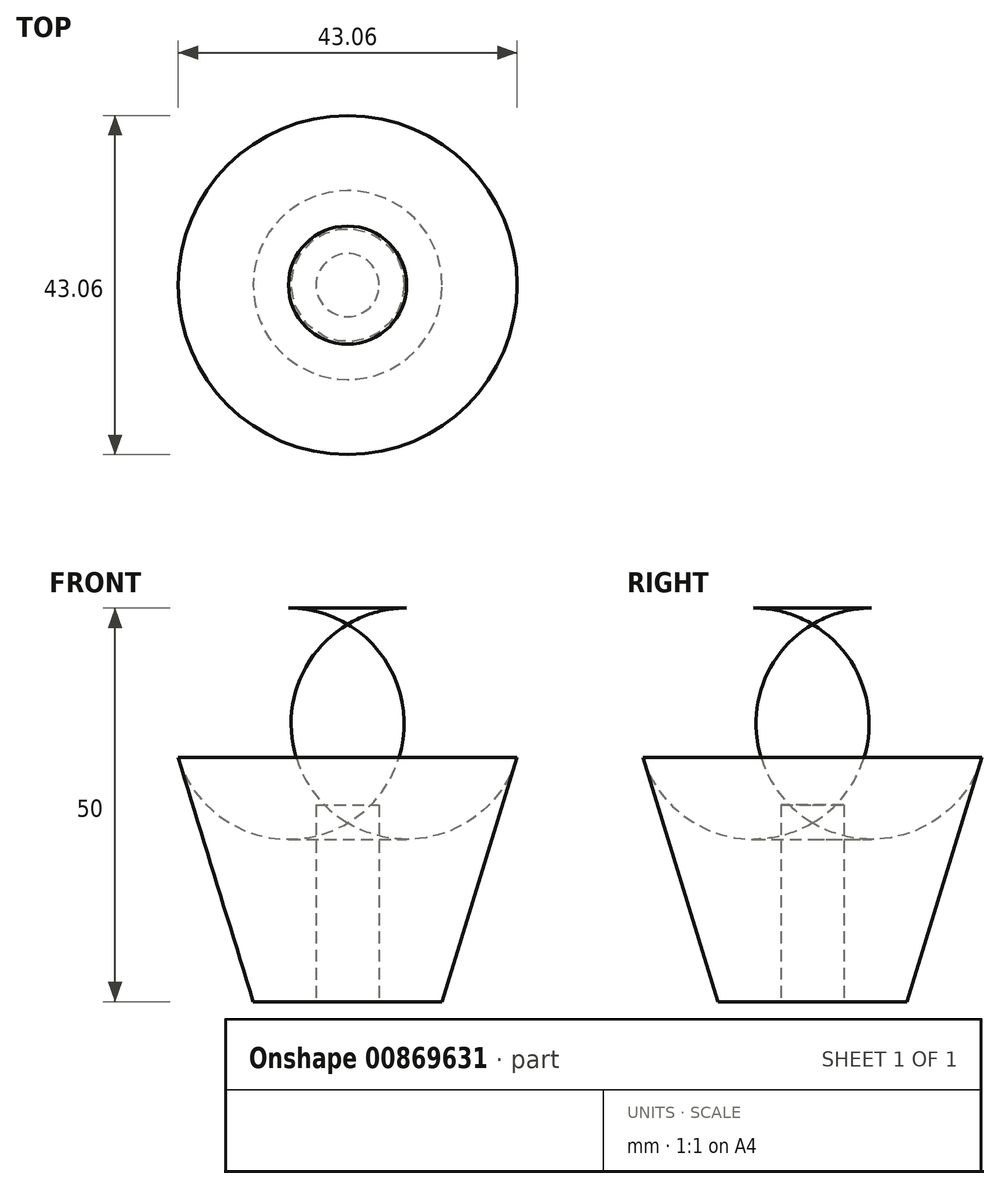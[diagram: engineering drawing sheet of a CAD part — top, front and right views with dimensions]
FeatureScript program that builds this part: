
annotation { "Feature Type Name" : "Feature", "Feature Type Description" : "" }
export const myFeature = defineFeature(function(context is Context, id is Id, definition is map)
    precondition{}
    {
        {
            var Q0;
            Q0=qCreatedBy(makeId("Front.planeOp"),FACE);
            var sketch = newSketch(context, id + "F0", { "sketchPlane" : qUnion([Q0])});
            skLineSegment(sketch, "E0", {"start": v(0, 0) * mm, "end": v(0, 50) * mm});
            skLineSegment(sketch, "E1", {"start": v(0, 50) * mm, "end": v(7.5, 50) * mm});
            skLineSegment(sketch, "E2", {"start": v(0, 0) * mm, "end": v(4, 0) * mm});
            skLineSegment(sketch, "E3", {"start": v(4, 0) * mm, "end": v(4, 25) * mm});
            skPoint(sketch, "E3.endSnap0", {"position": v(0, 25) * mm});
            skLineSegment(sketch, "E4", {"start": v(4, 25) * mm, "end": v(0, 25) * mm});
            skLineSegment(sketch, "E5", {"start": v(4, 0) * mm, "end": v(12, 0) * mm});
            skLineSegment(sketch, "E6", {"start": v(0, 25) * mm, "end": v(0, 31) * mm});
            skArc(sketch, "E7", {"start": v(21.53, 31) * mm, "mid": v(19.31, 44.04) * mm, "end": v(7.5, 50) * mm});
            skLineSegment(sketch, "E8", {"start": v(12, 0) * mm, "end": v(21.53, 31) * mm});
            skLineSegment(sketch, "E9", {"start": v(0, 31) * mm, "end": v(21.53, 31) * mm});
            skPoint(sketch, "E10.endSnap0", {"position": v(8, 0) * mm});
            skSolve(sketch);
        }
        {
            var Q0;
            {var subQ2=sQuery(id+"F0.wireOp",EDGE,"E1");Q0=makeQuery(id+"F0.imprint","IMPRINT",FACE,{"disambiguationData":[TD([[makeQuery(id+"F0.imprint","IMPRINT",EDGE,{"derivedFrom":subQ2}),-1.0]])]});}
            var Q1;
            Q1=makeQuery(id+"F0.imprint","IMPRINT",FACE,{"disambiguationData":[TD([[makeQuery(id+"F0.imprint","IMPRINT",EDGE,{"derivedFrom":sQuery(id+"F0.wireOp",EDGE,"E3")}),-1.0]])]});
            var Q2;
            Q2=sQuery(id+"F0.wireOp",EDGE,"E0");
            revolve(context, id + "F1", {"surfaceOperationType" : NewSurfaceOperationType.NEW, "entities" : qUnion([Q0, Q1]), "axis" : qUnion([Q2]), "revolveType" : RevolveType.FULL});
        }
    });
